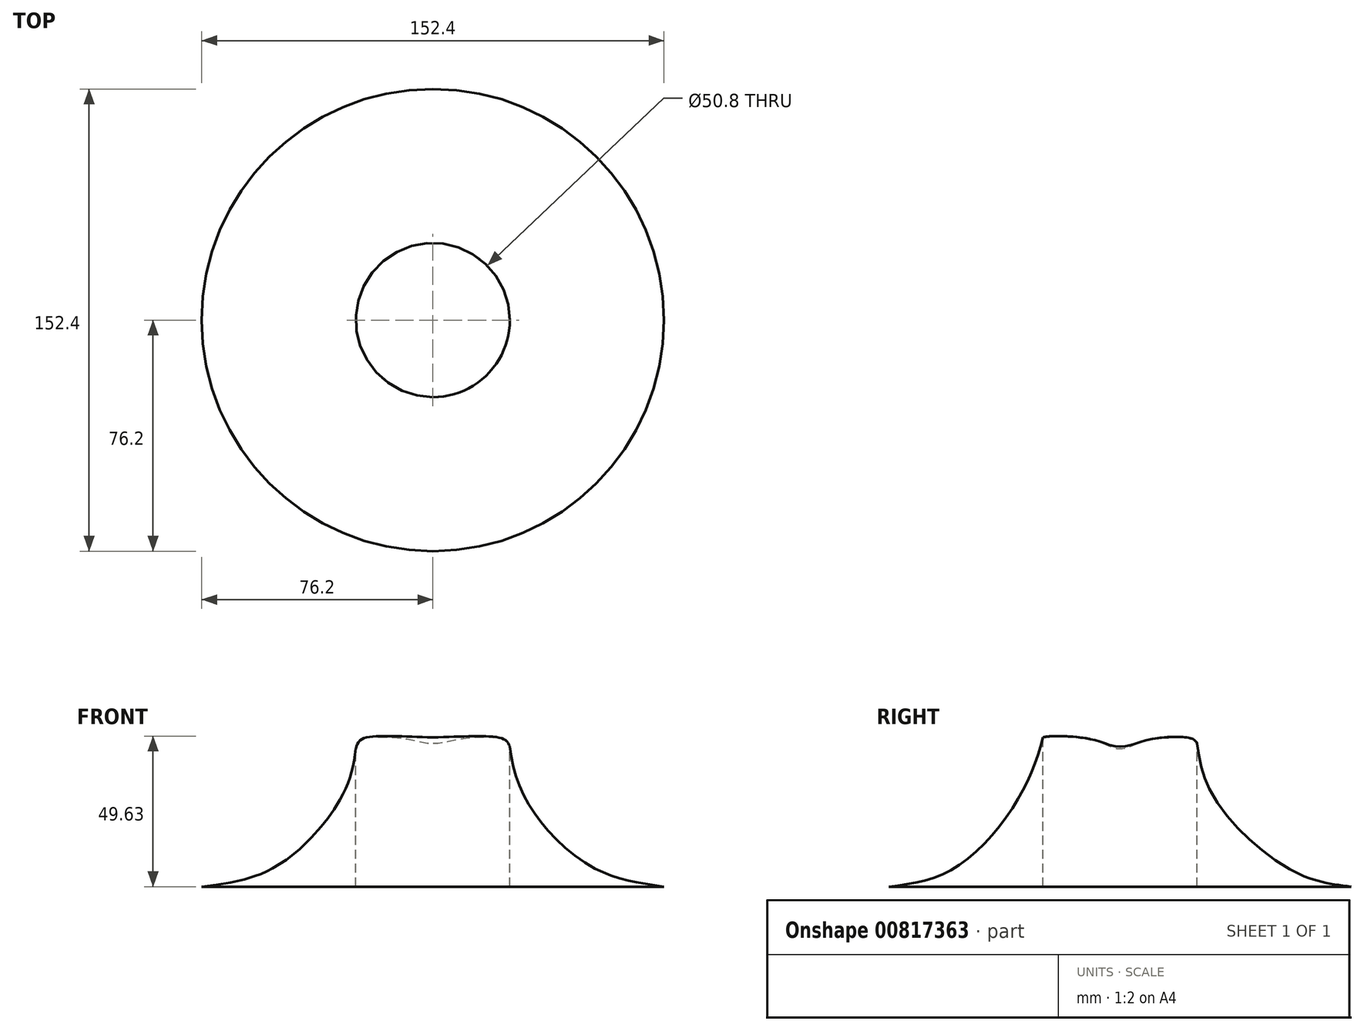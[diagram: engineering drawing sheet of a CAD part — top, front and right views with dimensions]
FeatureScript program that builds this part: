
annotation { "Feature Type Name" : "Feature", "Feature Type Description" : "" }
export const myFeature = defineFeature(function(context is Context, id is Id, definition is map)
    precondition{}
    {
        {
            var Q0;
            Q0=qCreatedBy(makeId("Top.planeOp"),FACE);
            var sketch = newSketch(context, id + "F0", { "sketchPlane" : qUnion([Q0])});
            skCircle(sketch, "E0", {"center": v(0, 0) * mm, "radius": 76.2 * mm});
            skPoint(sketch, "E1", {"position": v(76.2, 0) * mm});
            skPoint(sketch, "E2", {"position": v(-76.2, 0) * mm});
            skPoint(sketch, "E3", {"position": v(0, -76.2) * mm});
            skPoint(sketch, "E4", {"position": v(0, 76.2) * mm});
            skSolve(sketch);
        }
        {
            var Q0;
            Q0=qCreatedBy(makeId("Top.planeOp"),FACE);
            cPlane(context, id + "F1", {"entities" : qUnion([Q0]), "cplaneType" : CPlaneType.OFFSET, "offset" : 50.8 * mm, "width" : 152.4 * mm, "height" : 152.4 * mm});
        }
        {
            var Q0;
            Q0=qCreatedBy(id+"F1.planeOp",FACE);
            var sketch = newSketch(context, id + "F2", { "sketchPlane" : qUnion([Q0])});
            skCircle(sketch, "E5", {"center": v(0, 0) * mm, "radius": 24.98 * mm});
            skPoint(sketch, "E6", {"position": v(24.98, 0) * mm});
            skPoint(sketch, "E7", {"position": v(-24.98, 0) * mm});
            skPoint(sketch, "E8", {"position": v(0, -24.98) * mm});
            skPoint(sketch, "E9", {"position": v(0, 24.98) * mm});
            skSolve(sketch);
        }
        {
            var Q0;
            Q0=qCreatedBy(makeId("Front.planeOp"),FACE);
            var sketch = newSketch(context, id + "F3", { "sketchPlane" : qUnion([Q0])});
            skFitSpline(sketch, "E10", {"points": [v(76.2, 0) * mm, v(51.88, 6.82) * mm, v(29.9, 30.22) * mm, v(24.98, 50.8) * mm], "startDerivative": vector(-74.27, 10.56) * mm, "endDerivative": vector(-4.93, 68.22) * mm});
            skSolve(sketch);
        }
        {
            var Q0;
            Q0=qCreatedBy(makeId("Front.planeOp"),FACE);
            var sketch = newSketch(context, id + "F4", { "sketchPlane" : qUnion([Q0])});
            skFitSpline(sketch, "E11", {"points": [v(-76.2, 0) * mm, v(-51.4, 6.82) * mm, v(-28.95, 31.87) * mm, v(-24.98, 50.8) * mm], "startDerivative": vector(74.94, 9.2) * mm, "endDerivative": vector(4.24, 63.31) * mm});
            skSolve(sketch);
        }
        {
            var Q0;
            Q0=qCreatedBy(makeId("Right.planeOp"),FACE);
            var sketch = newSketch(context, id + "F5", { "sketchPlane" : qUnion([Q0])});
            skFitSpline(sketch, "E12", {"points": [v(76.2, 0) * mm, v(56.37, 5.44) * mm, v(30.14, 30.73) * mm, v(24.98, 50.8) * mm], "startDerivative": vector(-63.97, 7.68) * mm, "endDerivative": vector(-7.7, 65.02) * mm});
            skSolve(sketch);
        }
        {
            var Q0;
            Q0=qCreatedBy(makeId("Right.planeOp"),FACE);
            var sketch = newSketch(context, id + "F6", { "sketchPlane" : qUnion([Q0])});
            skFitSpline(sketch, "E13", {"points": [v(-76.2, 0) * mm, v(-54.97, 5.9) * mm, v(-33.7, 28.84) * mm, v(-24.98, 50.8) * mm], "startDerivative": vector(69.44, 9) * mm, "endDerivative": vector(18.22, 69.23) * mm});
            skSolve(sketch);
        }
        {
            var Q0;
            Q0=makeQuery(id+"F0.imprint","IMPRINT",FACE,{"disambiguationData":[TD([[makeQuery(id+"F0.imprint","IMPRINT",EDGE,{"derivedFrom":sQuery(id+"F0.wireOp",EDGE,"E0")}),1.0]])]});
            var Q1;
            Q1=makeQuery(id+"F2.imprint","IMPRINT",FACE,{"disambiguationData":[TD([[makeQuery(id+"F2.imprint","IMPRINT",EDGE,{"derivedFrom":sQuery(id+"F2.wireOp",EDGE,"E5")}),1.0]])]});
            var Q2;
            Q2=sQuery(id+"F5.wireOp",EDGE,"E12");
            var Q3;
            Q3=sQuery(id+"F4.wireOp",EDGE,"E11");
            var Q4;
            Q4=sQuery(id+"F6.wireOp",EDGE,"E13");
            var Q5;
            Q5=sQuery(id+"F3.wireOp",EDGE,"E10");
            loft(context, id + "F7", {"addGuides" : true, "sheetProfilesArray" : [{ "sheetProfileEntities" : qUnion([Q0]) }, { "sheetProfileEntities" : qUnion([Q1]) }], "guidesArray" : [{ "guideEntities" : qUnion([Q2]), "guideDerivativeType" : LoftGuideDerivativeType.DEFAULT, "guideDerivativeMagnitude" : 1 }, { "guideEntities" : qUnion([Q3]), "guideDerivativeType" : LoftGuideDerivativeType.DEFAULT, "guideDerivativeMagnitude" : 1 }, { "guideEntities" : qUnion([Q4]), "guideDerivativeType" : LoftGuideDerivativeType.DEFAULT, "guideDerivativeMagnitude" : 1 }, { "guideEntities" : qUnion([Q5]), "guideDerivativeType" : LoftGuideDerivativeType.DEFAULT, "guideDerivativeMagnitude" : 1 }]});
        }
        {
            var Q0;
            Q0=makeQuery(id+"F7.opLoft","CAP_FACE",FACE,{"disambiguationData":[OSD([makeQuery(id+"F2.imprint","IMPRINT",FACE,{"disambiguationData":[TD([[makeQuery(id+"F2.imprint","IMPRINT",EDGE,{"derivedFrom":sQuery(id+"F2.wireOp",EDGE,"E5")}),1.0]])]})])],"isStart":true});
            var sketch = newSketch(context, id + "F8", { "sketchPlane" : qUnion([Q0])});
            skPoint(sketch, "E14", {"position": v(0, 0) * mm});
            skSolve(sketch);
        }
        {
            var Q0;
            Q0=sQuery(id+"F8.wireOp",VERTEX,"E14");
            var Q1;
            Q1=makeQuery(id+"F7.opLoft","SWEPT_BODY",BODY,{"disambiguationData":[OSD([makeQuery(id+"F0.imprint","IMPRINT",FACE,{"disambiguationData":[TD([[makeQuery(id+"F0.imprint","IMPRINT",EDGE,{"derivedFrom":sQuery(id+"F0.wireOp",EDGE,"E0")}),1.0]])]}),makeQuery(id+"F2.imprint","IMPRINT",FACE,{"disambiguationData":[TD([[makeQuery(id+"F2.imprint","IMPRINT",EDGE,{"derivedFrom":sQuery(id+"F2.wireOp",EDGE,"E5")}),1.0]])]}),sQuery(id+"F3.wireOp",EDGE,"E10"),sQuery(id+"F4.wireOp",EDGE,"E11"),sQuery(id+"F5.wireOp",EDGE,"E12"),sQuery(id+"F6.wireOp",EDGE,"E13")])]});
            hole(context, id + "F9", {"style" : HoleStyle.SIMPLE, "endStyle" : HoleEndStyle.THROUGH, "holeDiameter" : 50.8 * mm, "majorDiameter" : 6.35 * mm, "isTappedThrough" : true, "tappedDepth" : 12.7 * mm, "tapClearance" : 3, "locations" : qUnion([Q0]), "scope" : qUnion([Q1])});
        }
    });
